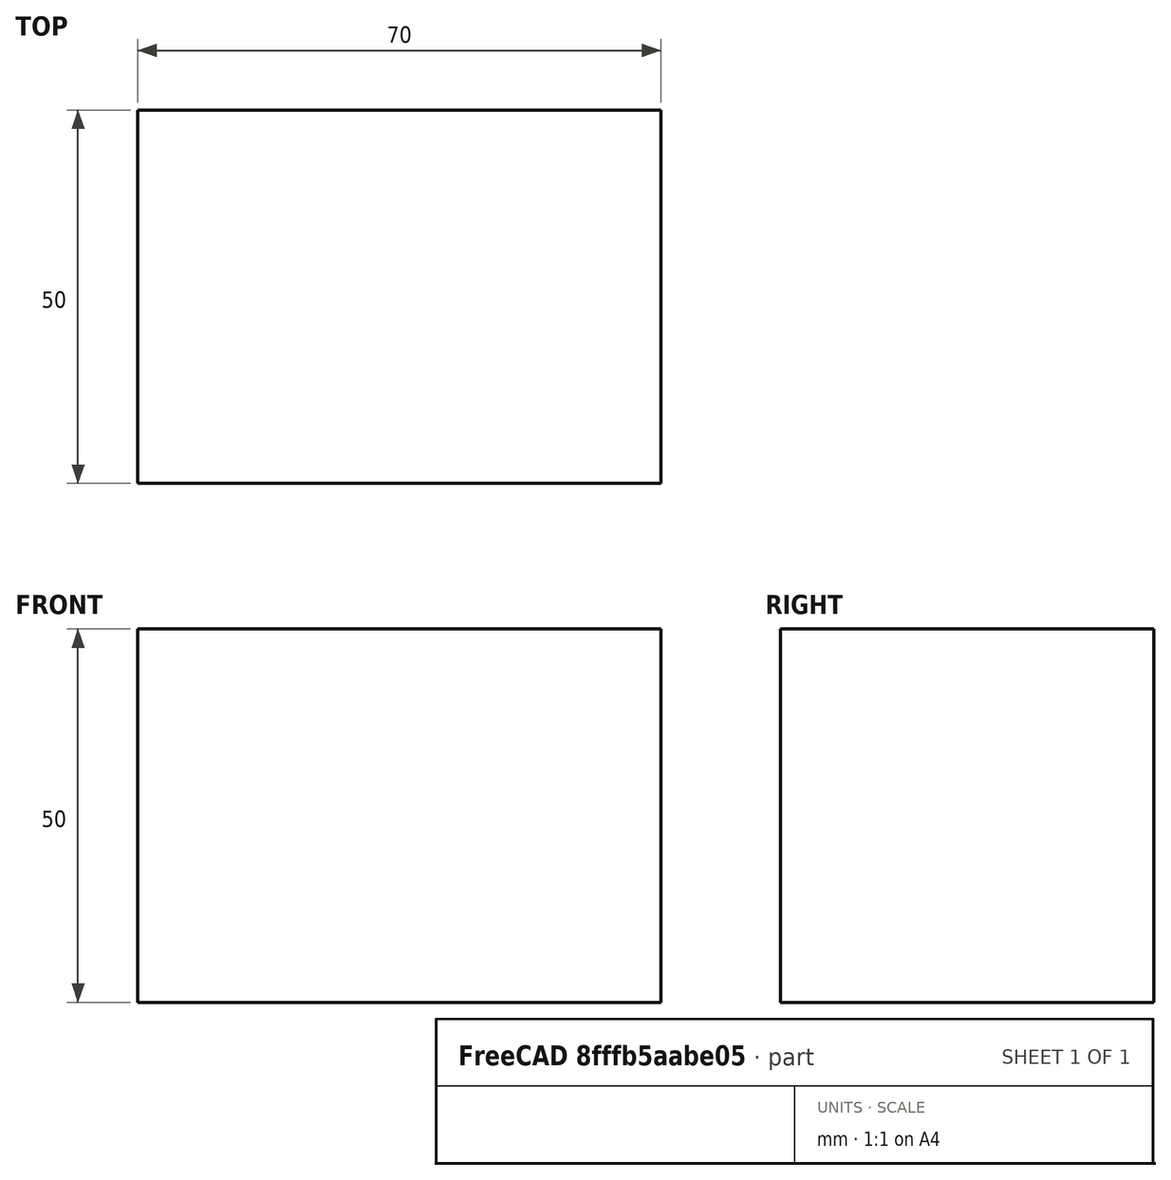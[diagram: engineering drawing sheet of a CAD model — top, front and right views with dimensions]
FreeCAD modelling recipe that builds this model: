
FCSTD DOCUMENT  (FreeCAD 0.15R4671 (Git))
Label: Flat Bar 70x50 EN10058 S235JR
License: All rights reserved
LicenseURL: http://en.wikipedia.org/wiki/All_rights_reserved
objects: Sketcher::SketchObject×1, Part::Extrusion×1
note: 2 computed .brp shape members not serialized (recipe doc carries the construction recipe); baked Part::Feature solids carry a one-line shape summary decoded from their .brp

FEATURE [Sketcher::SketchObject] Sketch
  sketch-geometry (4):
    g0: LineSegment StartX=-35 StartY=-25 StartZ=0 EndX=35 EndY=-25 EndZ=0
    g1: LineSegment StartX=35 StartY=-25 StartZ=0 EndX=35 EndY=25 EndZ=0
    g2: LineSegment StartX=35 StartY=25 StartZ=0 EndX=-35 EndY=25 EndZ=0
    g3: LineSegment StartX=-35 StartY=25 StartZ=0 EndX=-35 EndY=-25 EndZ=0
  constraints (12):
    c: Coincident(g0,g1)
    c: Coincident(g1,g2)
    c: Coincident(g2,g3)
    c: Coincident(g3,g0)
    c: Horizontal(g0)
    c: Horizontal(g2)
    c: Vertical(g1)
    c: Vertical(g3)
    c: Symmetric(g1,g2,g-2)
    c: Symmetric(g0,g1,g-1)
    c: DistanceY(g1) = 50
    c: DistanceX(g0) = 70
FEATURE [Part::Extrusion] Extrude  label="Flat Bar 70x50 EN10058 S235JR"
  Base = -> Sketch
  Dir = (0,0,50)
  Solid = true
